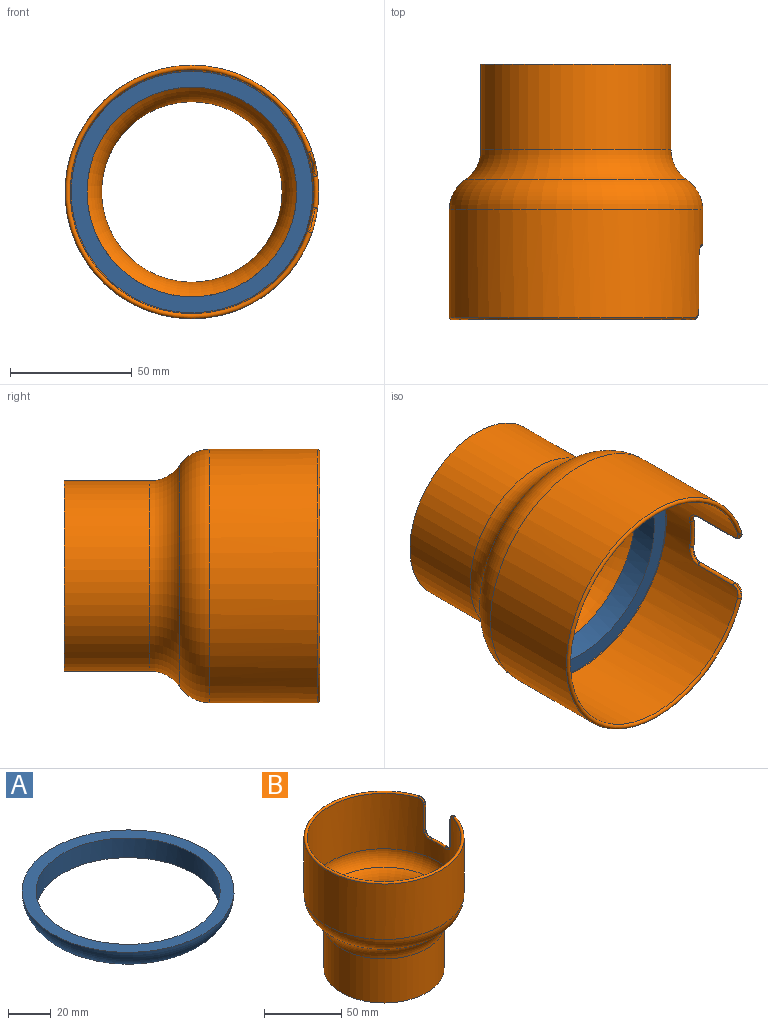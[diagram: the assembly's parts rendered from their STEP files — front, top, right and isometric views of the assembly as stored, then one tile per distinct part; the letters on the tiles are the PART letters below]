
ASSEMBLY  parts=2 mates=1
PART A: 3 faces, bbox 107.2x107.2x22.2 mm
  f0: torus R=36.5mm, axis (0,0,1), area 4041.7mm2, adj f1,f2
  f1: plane 99x99mm, normal (0,0,1), area 1888.9mm2, adj f0,f2
  f2: cylinder r=43mm len=86mm, axis (0,0,-1), area 3041.7mm2, adj f0,f1
PART B: 21 faces, bbox 116.9x116.9x104.7 mm
  f0: cylinder r=50mm len=100mm, axis (0,0,1), area 13088.7mm2, adj f6,f9,f12,f13,f14,f15,f18,f19
  f1: cylinder r=52mm len=104mm, axis (0,0,1), area 13612.2mm2, adj f7,f9,f10,f11,f13,f14,f16,f17
  f2: cylinder r=39mm len=78mm, axis (0,0,1), area 8576.5mm2, adj f3,f8
  f3: plane 78x78mm, normal (0,0,-1), area 477.5mm2, adj f2,f4
  f4: cylinder r=37mm len=74mm, axis (0,0,1), area 8136.7mm2, adj f3,f5
  f5: torus R=54mm, axis (0,0,1), area 4089.2mm2, adj f4,f6
  f6: torus R=37mm, axis (0,0,1), area 3801.4mm2, adj f0,f5
  f7: torus R=37mm, axis (0,0,1), area 4541.6mm2, adj f1,f8
  f8: torus R=54mm, axis (0,0,1), area 3763.4mm2, adj f2,f7
  f9: torus R=51mm, axis (0,0,-1), area 901.1mm2, adj f0,f1,f10,f11,f12,f15
  f10: bspline ~6.48x6.17mm, area 13.1mm2, adj f1,f9,f12,f13
  f11: bspline ~6.48x6.17mm, area 13.1mm2, adj f1,f9,f14,f15
  f12: bspline ~6.18x6.11mm, area 10.3mm2, adj f0,f9,f10,f13
  f13: cylinder r=1mm len=20mm, axis (0,0,1), area 62.8mm2, adj f0,f1,f10,f12,f16,f18
  f14: cylinder r=1mm len=20mm, axis (0,0,1), area 62.8mm2, adj f0,f1,f11,f15,f17,f20
  f15: bspline ~6.18x5.29mm, area 10.3mm2, adj f0,f9,f11,f14
  f16: bspline ~7.47x7.31mm, area 14.6mm2, adj f1,f13,f18,f19
  f17: bspline ~7.47x7.31mm, area 14.6mm2, adj f1,f14,f19,f20
  f18: bspline ~7.31x7.19mm, area 12.1mm2, adj f0,f13,f16,f19
  f19: torus R=51mm, axis (0,0,1), area 41mm2, adj f0,f1,f16,f17,f18,f20
  f20: bspline ~7.19x6.33mm, area 12.1mm2, adj f0,f14,f17,f19
PLACE A rot(axis=(1,0,0),90deg) t=(0,-59.75,0)mm
PLACE B rot(axis=(1,0,0),90deg) t=(0,-59.72,0)mm
MATE slider B.f0 <-> A.f2  axis (0,-1,0) through (0,-35,0)mm
